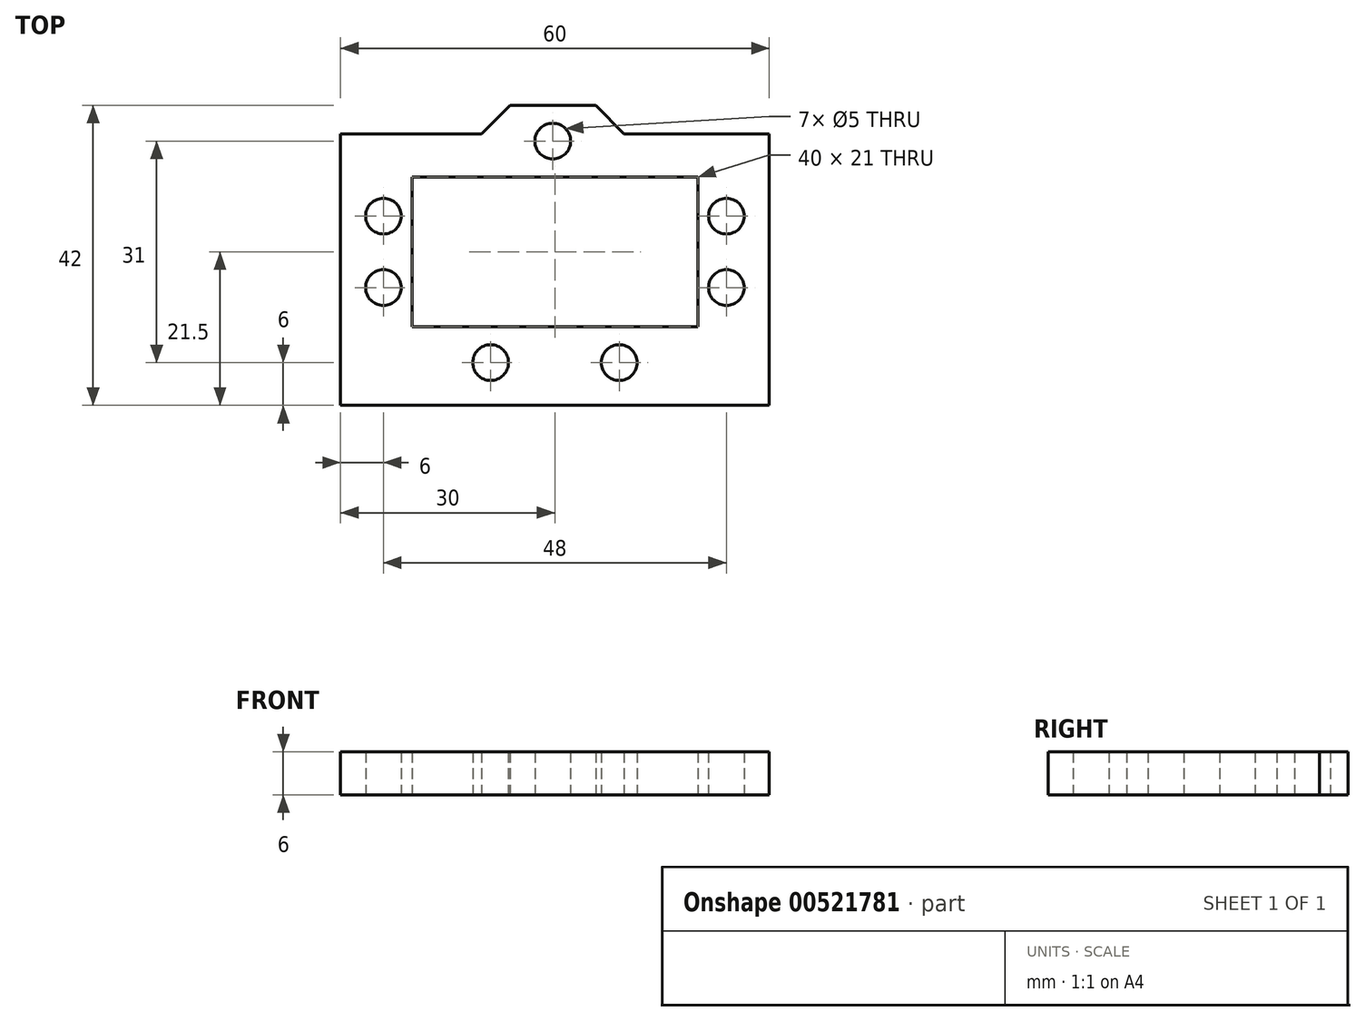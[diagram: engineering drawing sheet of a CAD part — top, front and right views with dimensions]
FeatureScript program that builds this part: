
annotation { "Feature Type Name" : "Feature", "Feature Type Description" : "" }
export const myFeature = defineFeature(function(context is Context, id is Id, definition is map)
    precondition{}
    {
        {
            var Q0;
            Q0=qCreatedBy(makeId("Top.planeOp"),FACE);
            var sketch = newSketch(context, id + "F0", { "sketchPlane" : qUnion([Q0])});
            skLineSegment(sketch, "E0.bottom", {"start": v(20, 10.5) * mm, "end": v(-20, 10.5) * mm});
            skLineSegment(sketch, "E0.top", {"start": v(20, -10.5) * mm, "end": v(-20, -10.5) * mm});
            skLineSegment(sketch, "E0.left", {"start": v(20, 10.5) * mm, "end": v(20, -10.5) * mm});
            skLineSegment(sketch, "E0.right", {"start": v(-20, 10.5) * mm, "end": v(-20, -10.5) * mm});
            skPoint(sketch, "E0.middle", {"position": v(0, 0) * mm});
            skLineSegment(sketch, "E1.0", {"start": v(19.4, 16.5) * mm, "end": v(9.7, 16.5) * mm});
            skLineSegment(sketch, "E2.0", {"start": v(20, -22.5) * mm, "end": v(-20, -22.5) * mm});
            skLineSegment(sketch, "E3.0", {"start": v(-30, 10.5) * mm, "end": v(-30, -10.5) * mm});
            skLineSegment(sketch, "E4.0", {"start": v(30, 10.5) * mm, "end": v(30, -10.5) * mm});
            skLineSegment(sketch, "E5", {"start": v(-20, 16.5) * mm, "end": v(-30, 16.5) * mm});
            skLineSegment(sketch, "E6", {"start": v(-30, 16.5) * mm, "end": v(-30, 10.5) * mm});
            skLineSegment(sketch, "E7", {"start": v(-30, -10.5) * mm, "end": v(-30, -22.5) * mm});
            skLineSegment(sketch, "E8", {"start": v(-30, -22.5) * mm, "end": v(-20, -22.5) * mm});
            skLineSegment(sketch, "E9", {"start": v(20, -22.5) * mm, "end": v(30, -22.5) * mm});
            skLineSegment(sketch, "E10", {"start": v(30, -22.5) * mm, "end": v(30, -10.5) * mm});
            skLineSegment(sketch, "E11", {"start": v(30, 10.5) * mm, "end": v(30, 16.5) * mm});
            skLineSegment(sketch, "E12", {"start": v(30, 16.5) * mm, "end": v(19.4, 16.5) * mm});
            skPoint(sketch, "E13", {"position": v(0, -10.5) * mm});
            skPoint(sketch, "E14", {"position": v(-9, -10.5) * mm});
            skPoint(sketch, "E15", {"position": v(9, -10.5) * mm});
            skPoint(sketch, "E16", {"position": v(-9, -15.5) * mm});
            skPoint(sketch, "E17", {"position": v(9, -15.5) * mm});
            skCircle(sketch, "E18", {"center": v(-9, -15.5) * mm, "radius": 2.5 * mm});
            skCircle(sketch, "E19", {"center": v(9, -15.5) * mm, "radius": 2.5 * mm});
            skPoint(sketch, "E20", {"position": v(-20, 0) * mm});
            skPoint(sketch, "E21", {"position": v(-20, 5) * mm});
            skPoint(sketch, "E22", {"position": v(-20, -5) * mm});
            skPoint(sketch, "E23", {"position": v(20, 0) * mm});
            skPoint(sketch, "E24", {"position": v(20, 5) * mm});
            skPoint(sketch, "E25", {"position": v(20, -5) * mm});
            skPoint(sketch, "E26", {"position": v(-24, -5) * mm});
            skPoint(sketch, "E27", {"position": v(-24, 5) * mm});
            skPoint(sketch, "E28", {"position": v(24, 5) * mm});
            skPoint(sketch, "E29", {"position": v(24, -5) * mm});
            skCircle(sketch, "E30", {"center": v(-24, 5) * mm, "radius": 2.5 * mm});
            skCircle(sketch, "E31", {"center": v(-24, -5) * mm, "radius": 2.5 * mm});
            skCircle(sketch, "E32", {"center": v(24, -5) * mm, "radius": 2.5 * mm});
            skCircle(sketch, "E33", {"center": v(24, 5) * mm, "radius": 2.5 * mm});
            skPoint(sketch, "E34", {"position": v(-0.3, 16.5) * mm});
            skPoint(sketch, "E35", {"position": v(-0.3, 20.5) * mm});
            skLineSegment(sketch, "E36.bottom", {"start": v(5.7, 20.5) * mm, "end": v(-6.3, 20.5) * mm});
            skPoint(sketch, "E37", {"position": v(-6.3, 16.5) * mm});
            skPoint(sketch, "E38", {"position": v(5.7, 16.5) * mm});
            skPoint(sketch, "E36.top.end.orphan", {"position": v(-6.3, 12.5) * mm});
            skPoint(sketch, "E39.orphan", {"position": v(5.7, 12.5) * mm});
            skPoint(sketch, "E40", {"position": v(-0.3, 15.5) * mm});
            skCircle(sketch, "E41", {"center": v(-0.3, 15.5) * mm, "radius": 2.5 * mm});
            skPoint(sketch, "E42", {"position": v(-10.3, 16.5) * mm});
            skPoint(sketch, "E43", {"position": v(9.7, 16.5) * mm});
            skLineSegment(sketch, "E44", {"start": v(-10.3, 16.5) * mm, "end": v(-6.3, 20.5) * mm});
            skLineSegment(sketch, "E45", {"start": v(5.7, 20.5) * mm, "end": v(9.7, 16.5) * mm});
            skPoint(sketch, "E46", {"position": v(-2.6, 16.5) * mm});
            skPoint(sketch, "E47", {"position": v(1.99, 16.5) * mm});
            skLineSegment(sketch, "E48.trimOffspring", {"start": v(-10.3, 16.5) * mm, "end": v(-20, 16.5) * mm});
            skSolve(sketch);
        }
        {
            var Q0;
            Q0=makeQuery(id+"F0.imprint","IMPRINT",FACE,{"disambiguationData":[TD([[makeQuery(id+"F0.imprint","IMPRINT",EDGE,{"derivedFrom":sQuery(id+"F0.wireOp",EDGE,"E0.bottom")}),-1.0]])]});
            extrude(context, id + "F1", {"entities" : qUnion([Q0]), "depth" : 6 * mm, "offsetDistance" : 25 * mm});
        }
        {
            var Q0;
            Q0=makeQuery(id+"F1.opExtrude","SWEPT_FACE",FACE,{"disambiguationData":[OSD([sQuery(id+"F0.wireOp",EDGE,"E2.0"),sQuery(id+"F0.wireOp",EDGE,"E8"),sQuery(id+"F0.wireOp",EDGE,"E9")])]});
            extrude(context, id + "F2", {"entities" : qUnion([Q0]), "operationType" : NewBodyOperationType.REMOVE, "oppositeDirection" : true, "depth" : 1 * mm, "offsetDistance" : 25 * mm});
        }
    });
